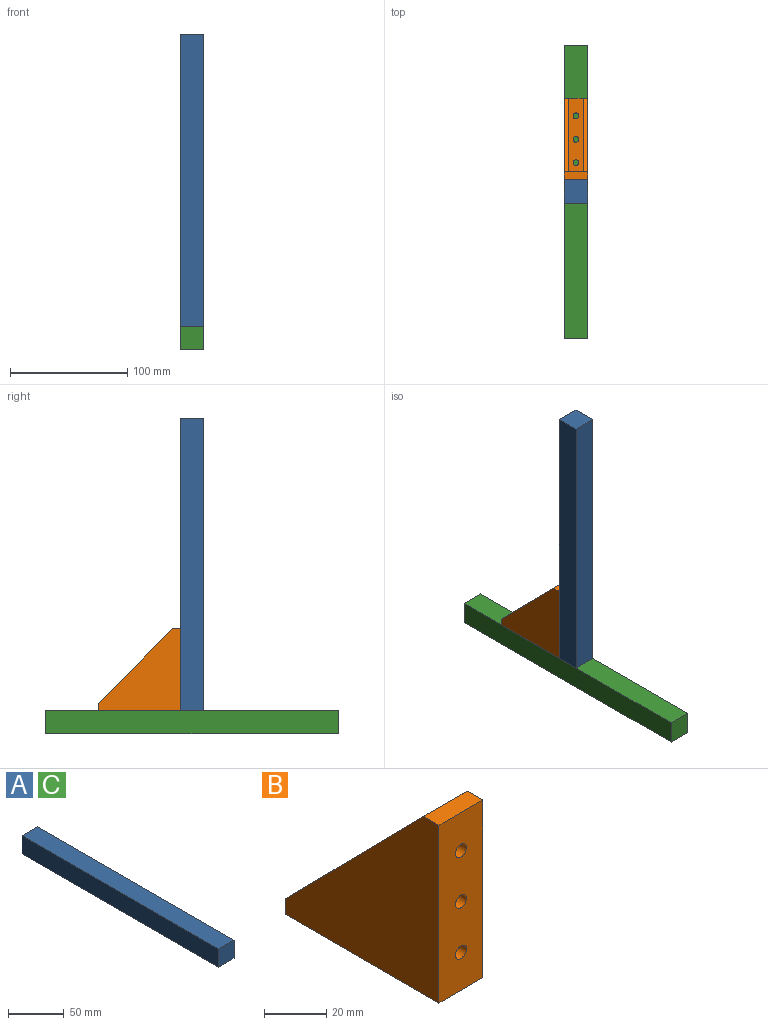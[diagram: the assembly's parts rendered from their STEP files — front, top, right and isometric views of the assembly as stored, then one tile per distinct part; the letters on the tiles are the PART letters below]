
ASSEMBLY  parts=3 mates=3
PART A: 6 faces, bbox 20x250x20 mm
  f0: plane 250x20mm, normal (1,0,0), area 5000mm2, adj f1,f3,f4,f5
  f1: plane 20x20mm, normal (0,1,0), area 400mm2, adj f0,f2,f4,f5
  f2: plane 250x20mm, normal (-1,0,0), area 5000mm2, adj f1,f3,f4,f5
  f3: plane 20x20mm, normal (0,-1,0), area 400mm2, adj f0,f2,f4,f5
  f4: plane 250x20mm, normal (0,0,1), area 5000mm2, adj f0,f1,f2,f3
  f5: plane 250x20mm, normal (0,0,-1), area 5000mm2, adj f0,f1,f2,f3
PART B: 18 faces, bbox 20x70x70 mm
  f0: plane 63x12mm, normal (0,0,1), area 697.1mm2, adj f1,f4,f5,f6,f7,f15,f17
  f1: plane 64x12mm, normal (0,1,0), area 709.1mm2, adj f0,f9,f11,f12,f13,f15,f17
  f2: plane 70x20.01mm, normal (0,-1,0), area 1341.9mm2, adj f3,f8,f9,f10,f11,f12,f13
  f3: plane 70x70mm, normal (1,0,0), area 2884mm2, adj f2,f4,f8,f9,f14
  f4: plane 20.01x6mm, normal (0,1,0), area 120.1mm2, adj f0,f3,f8,f10,f14,f16
  f5: cylinder r=2.5mm len=6mm, axis (0,0,-1), area 94.2mm2, adj f0,f8
  f6: cylinder r=2.5mm len=6mm, axis (0,0,-1), area 94.2mm2, adj f0,f8
  f7: cylinder r=2.5mm len=6mm, axis (0,0,-1), area 94.2mm2, adj f0,f8
  f8: plane 70x20.01mm, normal (0,0,-1), area 1341.9mm2, adj f2,f3,f4,f5,f6,f7,f10
  f9: plane 20.01x7mm, normal (0,0,1), area 140.1mm2, adj f1,f2,f3,f10,f14,f16
  f10: plane 70x70mm, normal (-1,0,0), area 2884mm2, adj f2,f4,f8,f9,f16
  f11: cylinder r=2.5mm len=7mm, axis (0,-1,0), area 110mm2, adj f1,f2
  f12: cylinder r=2.5mm len=7mm, axis (0,-1,0), area 110mm2, adj f1,f2
  f13: cylinder r=2.5mm len=7mm, axis (0,-1,0), area 110mm2, adj f1,f2
  f14: plane 64x63mm, normal (0,0.71,0.7), area 360.2mm2, adj f3,f4,f9,f15
  f15: plane 64x63mm, normal (-1,0,0), area 2016mm2, adj f0,f1,f14
  f16: plane 64x63mm, normal (0,0.71,0.7), area 359.2mm2, adj f4,f9,f10,f17
  f17: plane 64x63mm, normal (1,0,0), area 2016mm2, adj f0,f1,f16
PART C: same geometry as A
PLACE A rot(axis=(-0.58,0.58,-0.58),120deg) t=(120.84,-13.21,243.24)mm
PLACE B t=(130.86,31.79,118.24)mm
PLACE C t=(130.84,-13.21,98.24)mm
MATE planar B.f11 <-> A.f2  axis (0,-1,0) through (130.84,-3.21,173.24)mm
MATE planar A.f1 <-> C.f4  axis (0,0,-1) through (130.84,-13.21,118.24)mm
MATE planar B.f8 <-> C.f4  axis (0,0,-1) through (130.85,66.79,118.24)mm
